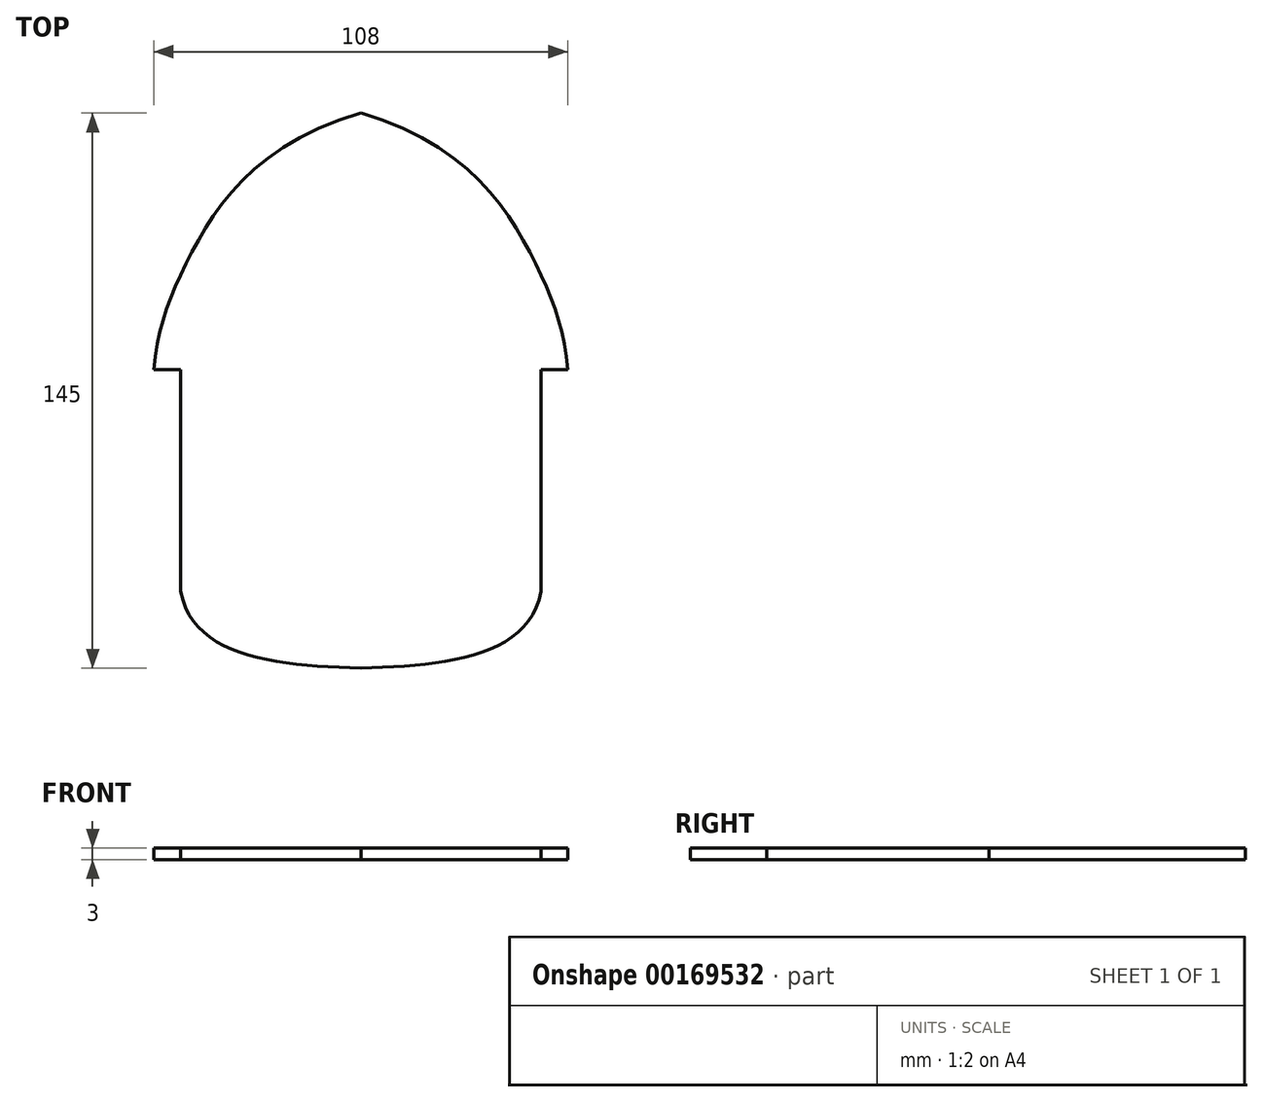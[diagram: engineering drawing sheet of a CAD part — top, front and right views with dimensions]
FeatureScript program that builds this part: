
annotation { "Feature Type Name" : "Feature", "Feature Type Description" : "" }
export const myFeature = defineFeature(function(context is Context, id is Id, definition is map)
    precondition{}
    {
        {
            var Q0;
            Q0=qCreatedBy(makeId("Top.planeOp"),FACE);
            var sketch = newSketch(context, id + "F0", { "sketchPlane" : qUnion([Q0])});
            skLineSegment(sketch, "E0.bottom", {"start": v(-66.85, 72.5) * mm, "end": v(-44.48, 72.5) * mm});
            skLineSegment(sketch, "E1", {"start": v(-54, 5.5) * mm, "end": v(53.54, 5.5) * mm});
            skPoint(sketch, "E2.orphan", {"position": v(-53.54, 72.5) * mm});
            skFitSpline(sketch, "E3", {"points": [v(0, 72.5) * mm, v(-44.48, 35.42) * mm, v(-54, 5.5) * mm], "startDerivative": vector(-140.73, -41.15) * mm, "endDerivative": vector(-6.52, -79.84) * mm});
            skPoint(sketch, "E4.end.orphan", {"position": v(-44.48, -1.66) * mm});
            skLineSegment(sketch, "E5", {"start": v(0, 72.5) * mm, "end": v(0, -72.5) * mm});
            skPoint(sketch, "E6.orphan", {"position": v(-43.82, -72.5) * mm});
            skPoint(sketch, "E0.top.end.orphan", {"position": v(43.82, -72.5) * mm});
            skFitSpline(sketch, "E7", {"points": [v(-47, -52.5) * mm, v(0, -72.5) * mm, v(47, -52.5) * mm], "startDerivative": vector(19.05, -103.8) * mm, "endDerivative": vector(19.05, 120) * mm});
            skLineSegment(sketch, "E8", {"start": v(-47, -52.5) * mm, "end": v(-47, 5.5) * mm});
            skSolve(sketch);
        }
        {
            var Q0;
            Q0=qSketchRegion(id+"F0",true);
            extrude(context, id + "F1", {"entities" : qUnion([Q0]), "depth" : 3 * mm});
        }
        {
            var Q0;
            Q0=makeQuery(id+"F1.opExtrude","SWEPT_BODY",BODY,{"disambiguationData":[OSD([sQuery(id+"F0.wireOp",EDGE,"1IXK0Z66-OG1G-Lh8k-BSXM-c3joX9Cgf9E4.top"),sQuery(id+"F0.wireOp",EDGE,"1IXK0Z66-OG1G-Lh8k-BSXM-c3joX9Cgf9E4.left"),sQuery(id+"F0.wireOp",EDGE,"E1"),sQuery(id+"F0.wireOp",EDGE,"E3"),sQuery(id+"F0.wireOp",EDGE,"E5")])]});
            var Q1;
            Q1=makeQuery(id+"F1.opExtrude","SWEPT_FACE",FACE,{"disambiguationData":[OSD([sQuery(id+"F0.wireOp",EDGE,"E5")])]});
            mirror(context, id + "F2", {"operationType" : NewBodyOperationType.ADD, "entities" : qUnion([Q0]), "mirrorPlane" : qUnion([Q1])});
        }
    });
